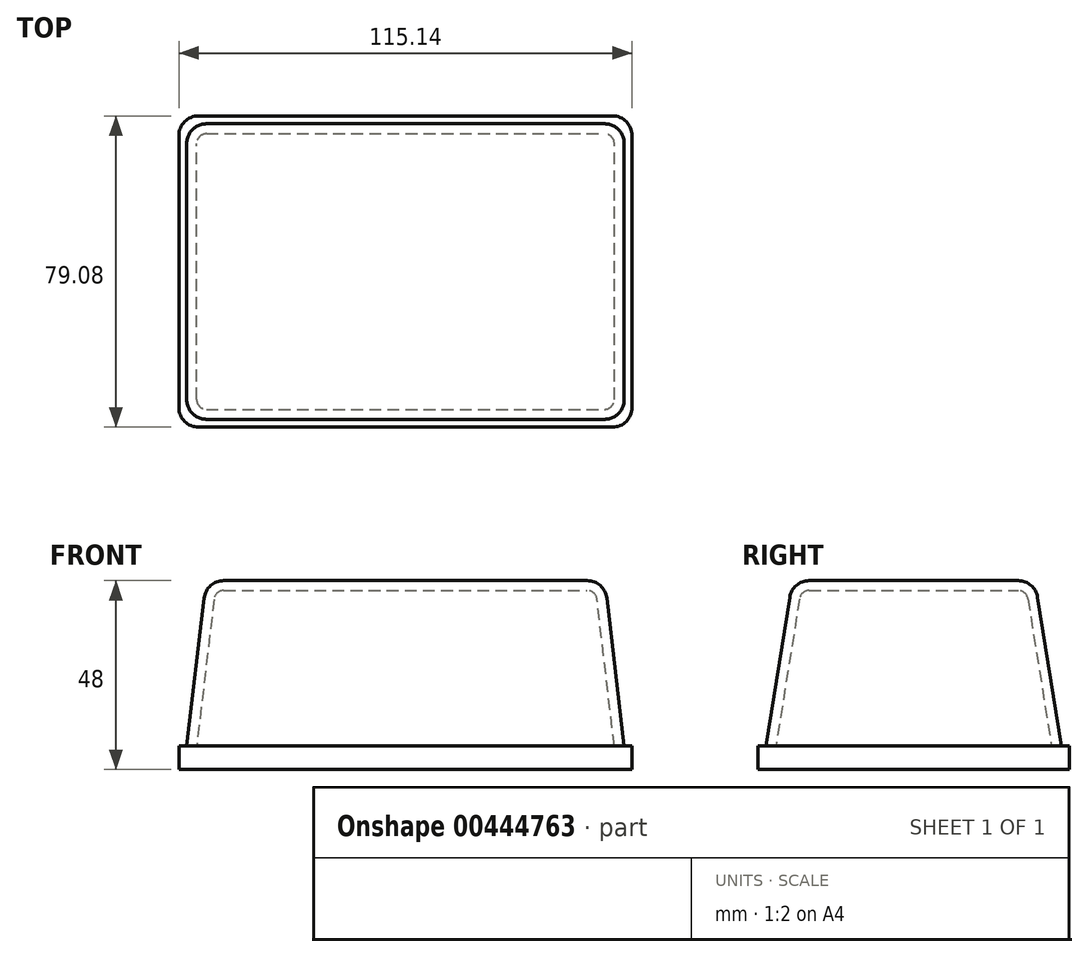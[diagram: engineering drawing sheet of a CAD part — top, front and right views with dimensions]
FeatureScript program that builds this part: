
annotation { "Feature Type Name" : "Feature", "Feature Type Description" : "" }
export const myFeature = defineFeature(function(context is Context, id is Id, definition is map)
    precondition{}
    {
        {
            var Q0;
            Q0=qCreatedBy(makeId("Top.planeOp"),FACE);
            var sketch = newSketch(context, id + "F0", { "sketchPlane" : qUnion([Q0])});
            skPoint(sketch, "E0.start.orphan", {"position": v(0, 46.8) * mm});
            skLineSegment(sketch, "E1", {"start": v(-55.57, 37.53) * mm, "end": v(55.57, 37.53) * mm});
            skLineSegment(sketch, "E2", {"start": v(55.57, -37.54) * mm, "end": v(-55.57, -37.54) * mm});
            skPoint(sketch, "E3.start.orphan", {"position": v(-55.57, 0) * mm});
            skLineSegment(sketch, "E4", {"start": v(-55.57, 37.53) * mm, "end": v(-55.57, -37.54) * mm});
            skPoint(sketch, "E5.start.orphan", {"position": v(55.57, 0) * mm});
            skLineSegment(sketch, "E6", {"start": v(55.57, 37.53) * mm, "end": v(55.57, -37.54) * mm});
            skSolve(sketch);
        }
        {
            var Q0;
            Q0=makeQuery(id+"F0.imprint","IMPRINT",FACE,{"disambiguationData":[TD([[makeQuery(id+"F0.imprint","IMPRINT",EDGE,{"derivedFrom":sQuery(id+"F0.wireOp",EDGE,"E1")}),-1.0]])]});
            cPlane(context, id + "F1", {"entities" : qUnion([Q0]), "cplaneType" : CPlaneType.OFFSET, "offset" : 42 * mm, "width" : 150 * mm, "height" : 150 * mm});
        }
        {
            var Q0;
            Q0=qCreatedBy(id+"F1.planeOp",FACE);
            var sketch = newSketch(context, id + "F2", { "sketchPlane" : qUnion([Q0])});
            skLineSegment(sketch, "E7.bottom", {"start": v(-50.6, -30.82) * mm, "end": v(50.61, -30.82) * mm});
            skLineSegment(sketch, "E7.top", {"start": v(-50.61, 30.82) * mm, "end": v(50.6, 30.82) * mm});
            skLineSegment(sketch, "E7.left", {"start": v(-50.6, -30.82) * mm, "end": v(-50.61, 30.82) * mm});
            skLineSegment(sketch, "E7.right", {"start": v(50.61, -30.82) * mm, "end": v(50.6, 30.82) * mm});
            skPoint(sketch, "E7.middle", {"position": v(0, 0) * mm});
            skSolve(sketch);
        }
        {
            var Q0;
            Q0=makeQuery(id+"F2.imprint","IMPRINT",FACE,{"disambiguationData":[TD([[makeQuery(id+"F2.imprint","IMPRINT",EDGE,{"derivedFrom":sQuery(id+"F2.wireOp",EDGE,"E7.bottom")}),1.0]])]});
            var Q1;
            Q1=makeQuery(id+"F0.imprint","IMPRINT",FACE,{"disambiguationData":[TD([[makeQuery(id+"F0.imprint","IMPRINT",EDGE,{"derivedFrom":sQuery(id+"F0.wireOp",EDGE,"E1")}),-1.0]])]});
            loft(context, id + "F3", {"sheetProfilesArray" : [{ "sheetProfileEntities" : qUnion([Q0]) }, { "sheetProfileEntities" : qUnion([Q1]) }]});
        }
        {
            var Q0;
            Q0=makeQuery(id+"F3.opLoft","SWEPT_EDGE",EDGE,{"disambiguationData":[OSD([sQuery(id+"F0.wireOp",EDGE,"E1"),sQuery(id+"F0.wireOp",EDGE,"E4"),sQuery(id+"F2.wireOp",EDGE,"E7.top"),sQuery(id+"F2.wireOp",EDGE,"E7.left")])]});
            var Q1;
            Q1=makeQuery(id+"F3.opLoft","SWEPT_EDGE",EDGE,{"disambiguationData":[OSD([sQuery(id+"F0.wireOp",EDGE,"E1"),sQuery(id+"F0.wireOp",EDGE,"E6"),sQuery(id+"F2.wireOp",EDGE,"E7.top"),sQuery(id+"F2.wireOp",EDGE,"E7.right")])]});
            var Q2;
            Q2=makeQuery(id+"F3.opLoft","SWEPT_EDGE",EDGE,{"disambiguationData":[OSD([sQuery(id+"F0.wireOp",EDGE,"E2"),sQuery(id+"F0.wireOp",EDGE,"E6"),sQuery(id+"F2.wireOp",EDGE,"E7.bottom"),sQuery(id+"F2.wireOp",EDGE,"E7.right")])]});
            var Q3;
            Q3=makeQuery(id+"F3.opLoft","SWEPT_EDGE",EDGE,{"disambiguationData":[OSD([sQuery(id+"F0.wireOp",EDGE,"E2"),sQuery(id+"F0.wireOp",EDGE,"E4"),sQuery(id+"F2.wireOp",EDGE,"E7.bottom"),sQuery(id+"F2.wireOp",EDGE,"E7.left")])]});
            var Q4;
            Q4=makeQuery(id+"F3.opLoft","MID_CAP_EDGE",EDGE,{"disambiguationData":[OSD([sQuery(id+"F2.wireOp",EDGE,"E7.bottom"),sQuery(id+"F2.wireOp",EDGE,"E7.left"),sQuery(id+"F2.wireOp",EDGE,"E7.right")])],"capPos":0.0});
            var Q5;
            Q5=makeQuery(id+"F3.opLoft","MID_CAP_EDGE",EDGE,{"disambiguationData":[OSD([sQuery(id+"F2.wireOp",EDGE,"E7.bottom"),sQuery(id+"F2.wireOp",EDGE,"E7.top"),sQuery(id+"F2.wireOp",EDGE,"E7.right")])],"capPos":0.0});
            var Q6;
            Q6=makeQuery(id+"F3.opLoft","MID_CAP_EDGE",EDGE,{"disambiguationData":[OSD([sQuery(id+"F2.wireOp",EDGE,"E7.top"),sQuery(id+"F2.wireOp",EDGE,"E7.left"),sQuery(id+"F2.wireOp",EDGE,"E7.right")])],"capPos":0.0});
            var Q7;
            Q7=makeQuery(id+"F3.opLoft","MID_CAP_EDGE",EDGE,{"disambiguationData":[OSD([sQuery(id+"F2.wireOp",EDGE,"E7.bottom"),sQuery(id+"F2.wireOp",EDGE,"E7.top"),sQuery(id+"F2.wireOp",EDGE,"E7.left")])],"capPos":0.0});
            fillet(context, id + "F4", {"entities" : qUnion([Q0, Q1, Q2, Q3, Q4, Q5, Q6, Q7]), "radius" : 5 * mm, "tangentPropagation" : true, "allowEdgeOverflow" : false});
        }
        {
            var Q0;
            Q0=makeQuery(id+"F3.opLoft","CAP_FACE",FACE,{"disambiguationData":[OSD([makeQuery(id+"F0.imprint","IMPRINT",FACE,{"disambiguationData":[TD([[makeQuery(id+"F0.imprint","IMPRINT",EDGE,{"derivedFrom":sQuery(id+"F0.wireOp",EDGE,"E1")}),-1.0]])]})])],"isStart":true});
            shell(context, id + "F5", {"entities" : qUnion([Q0]), "thickness" : 2.5 * mm});
        }
        {
            var Q0;
            Q0=makeQuery(id+"F3.opLoft","CAP_FACE",FACE,{"disambiguationData":[OSD([makeQuery(id+"F0.imprint","IMPRINT",FACE,{"disambiguationData":[TD([[makeQuery(id+"F0.imprint","IMPRINT",EDGE,{"derivedFrom":sQuery(id+"F0.wireOp",EDGE,"E1")}),-1.0]])]})])],"isStart":true});
            var sketch = newSketch(context, id + "F6", { "sketchPlane" : qUnion([Q0])});
            skPoint(sketch, "E8.startSnap0", {"position": v(55.57, 0) * mm});
            skLineSegment(sketch, "E9", {"start": v(8.28, -37.53) * mm, "end": v(8.28, -37.28) * mm});
            skPoint(sketch, "E10.end.orphan", {"position": v(8.28, 39.54) * mm});
            skLineSegment(sketch, "E11", {"start": v(-52.57, 39.54) * mm, "end": v(52.57, 39.54) * mm});
            skPoint(sketch, "E8.end.orphan", {"position": v(57.57, 3.4) * mm});
            skPoint(sketch, "E8.start.orphan", {"position": v(55.57, 3.4) * mm});
            skLineSegment(sketch, "E12", {"start": v(57.57, 34.54) * mm, "end": v(57.57, -34.53) * mm});
            skPoint(sketch, "E13.end.orphan", {"position": v(8.28, -39.53) * mm});
            skLineSegment(sketch, "E14", {"start": v(-52.57, -39.53) * mm, "end": v(52.57, -39.53) * mm});
            skPoint(sketch, "E15.end.orphan", {"position": v(-57.57, 3.4) * mm});
            skLineSegment(sketch, "E16", {"start": v(-57.57, 34.54) * mm, "end": v(-57.57, -34.53) * mm});
            skPoint(sketch, "E17.visualSharp", {"position": v(-57.57, 39.54) * mm});
            skArc(sketch, "E17.filletArc", {"start": v(-52.57, 39.54) * mm, "mid": v(-56.1, 38.07) * mm, "end": v(-57.57, 34.54) * mm});
            skPoint(sketch, "E18.visualSharp", {"position": v(57.57, 39.54) * mm});
            skArc(sketch, "E18.filletArc", {"start": v(57.57, 34.54) * mm, "mid": v(56.1, 38.07) * mm, "end": v(52.57, 39.54) * mm});
            skPoint(sketch, "E19.visualSharp", {"position": v(57.57, -39.53) * mm});
            skArc(sketch, "E19.filletArc", {"start": v(52.57, -39.53) * mm, "mid": v(56.1, -38.07) * mm, "end": v(57.57, -34.53) * mm});
            skPoint(sketch, "E20.visualSharp", {"position": v(-57.57, -39.53) * mm});
            skArc(sketch, "E20.filletArc", {"start": v(-57.57, -34.53) * mm, "mid": v(-56.1, -38.07) * mm, "end": v(-52.57, -39.53) * mm});
            skSolve(sketch);
        }
        {
            var Q0;
            Q0 = qSketchRegion(id + "F6", true);
            extrude(context, id + "F7", {"entities" : qUnion([Q0]), "operationType" : NewBodyOperationType.ADD, "depth" : 6 * mm});
        }
    });
